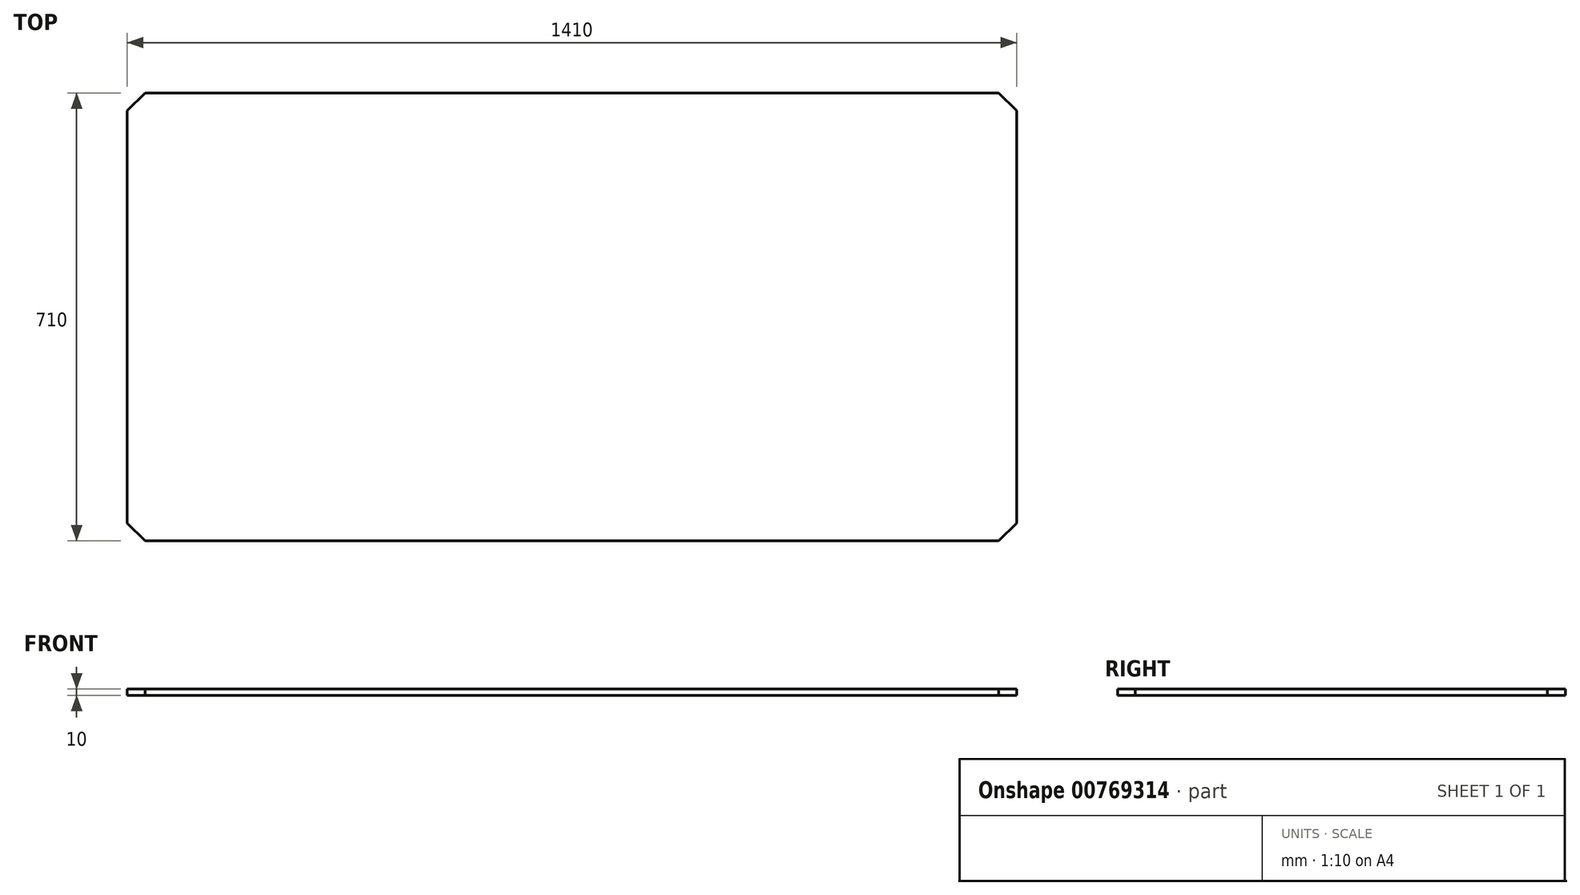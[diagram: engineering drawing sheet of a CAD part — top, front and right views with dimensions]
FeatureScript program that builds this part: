
annotation { "Feature Type Name" : "Feature", "Feature Type Description" : "" }
export const myFeature = defineFeature(function(context is Context, id is Id, definition is map)
    precondition{}
    {
        {
            var Q0;
            Q0=qCreatedBy(makeId("Top.planeOp"),FACE);
            var sketch = newSketch(context, id + "F0", { "sketchPlane" : qUnion([Q0])});
            skLineSegment(sketch, "E0.bottom", {"start": v(-705, 355) * mm, "end": v(705, 355) * mm});
            skLineSegment(sketch, "E0.top", {"start": v(-705, -355) * mm, "end": v(705, -355) * mm});
            skLineSegment(sketch, "E0.left", {"start": v(-705, 355) * mm, "end": v(-705, -355) * mm});
            skLineSegment(sketch, "E0.right", {"start": v(705, 355) * mm, "end": v(705, -355) * mm});
            skPoint(sketch, "E0.middle", {"position": v(0, 0) * mm});
            skLineSegment(sketch, "E1", {"start": v(-705, 326.72) * mm, "end": v(-676.72, 355) * mm});
            skLineSegment(sketch, "E2", {"start": v(676.72, 355) * mm, "end": v(705, 326.72) * mm});
            skLineSegment(sketch, "E3", {"start": v(676.72, -355) * mm, "end": v(705, -326.72) * mm});
            skLineSegment(sketch, "E4", {"start": v(-705, -326.72) * mm, "end": v(-676.72, -355) * mm});
            skSolve(sketch);
        }
        {
            var Q0;
            {var subQ3=sQuery(id+"F0.wireOp",EDGE,"E1");Q0=makeQuery(id+"F0.imprint","IMPRINT",FACE,{"disambiguationData":[TD([[makeQuery(id+"F0.imprint","IMPRINT",EDGE,{"derivedFrom":subQ3}),-1.0]])]});}
            extrude(context, id + "F1", {"entities" : qUnion([Q0]), "depth" : 10 * mm, "offsetDistance" : 25 * mm});
        }
    });
